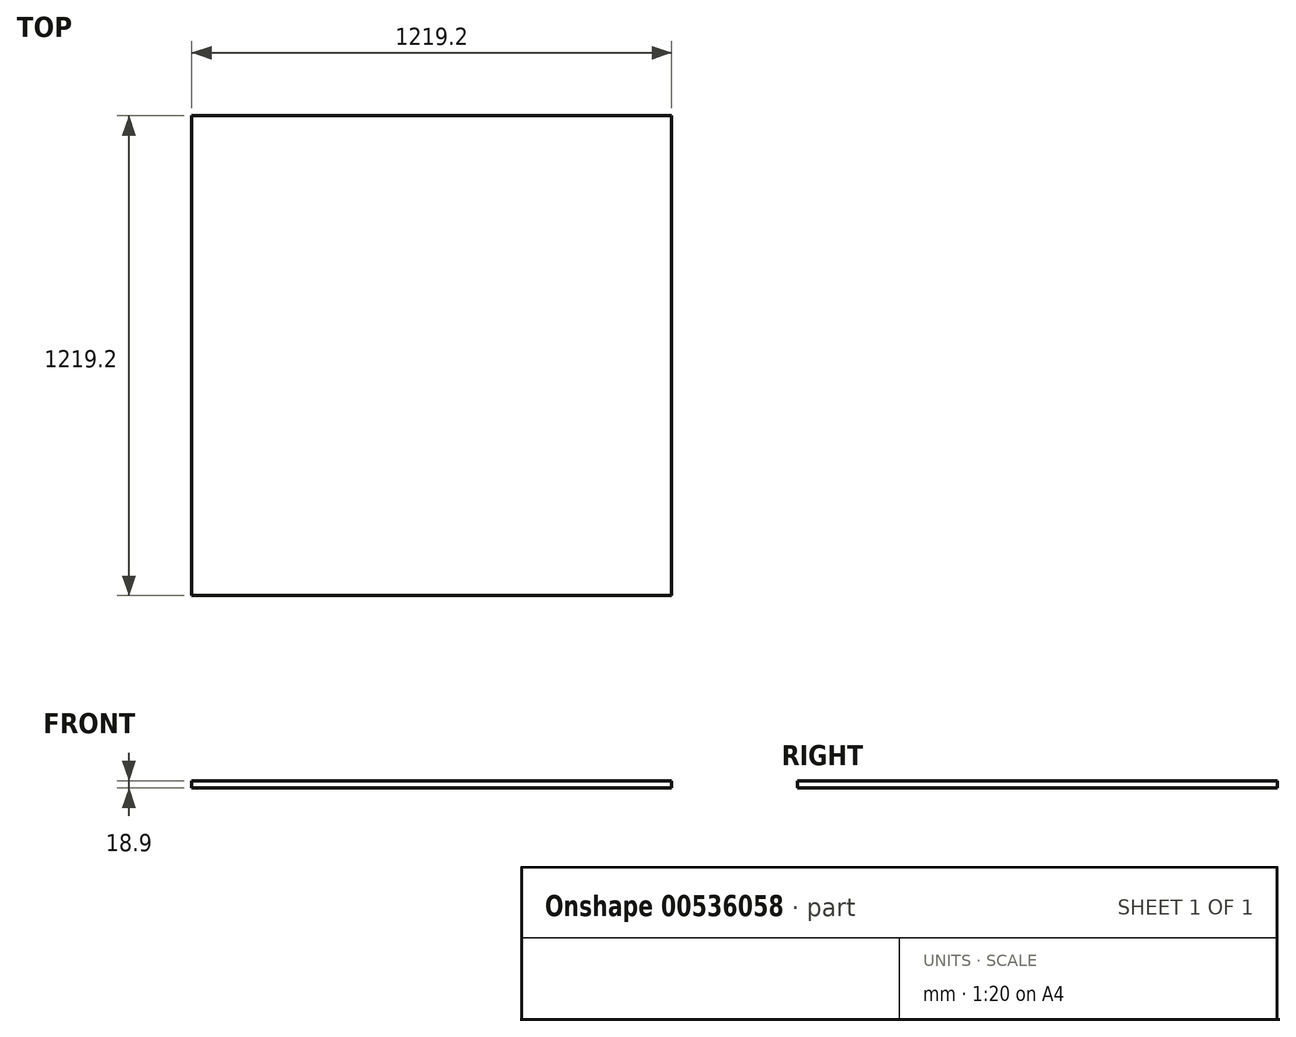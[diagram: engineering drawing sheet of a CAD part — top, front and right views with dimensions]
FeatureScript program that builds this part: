
annotation { "Feature Type Name" : "Feature", "Feature Type Description" : "" }
export const myFeature = defineFeature(function(context is Context, id is Id, definition is map)
    precondition{}
    {
        {
            var Q0;
            Q0=qCreatedBy(makeId("Top.planeOp"),FACE);
            var sketch = newSketch(context, id + "F0", { "sketchPlane" : qUnion([Q0])});
            skLineSegment(sketch, "E0.bottom", {"start": v(0, 0) * mm, "end": v(1219.2, 0) * mm});
            skLineSegment(sketch, "E0.top", {"start": v(0, 1219.2) * mm, "end": v(1219.2, 1219.2) * mm});
            skLineSegment(sketch, "E0.left", {"start": v(0, 0) * mm, "end": v(0, 1219.2) * mm});
            skLineSegment(sketch, "E0.right", {"start": v(1219.2, 0) * mm, "end": v(1219.2, 1219.2) * mm});
            skSolve(sketch);
        }
        {
            var Q0;
            Q0=makeQuery(id+"F0.imprint","IMPRINT",FACE,{"disambiguationData":[TD([[makeQuery(id+"F0.imprint","IMPRINT",EDGE,{"derivedFrom":sQuery(id+"F0.wireOp",EDGE,"E0.bottom")}),1.0]])]});
            extrude(context, id + "F1", {"entities" : qUnion([Q0]), "depth" : 18.9 * mm, "offsetDistance" : 30.48 * mm});
        }
    });
